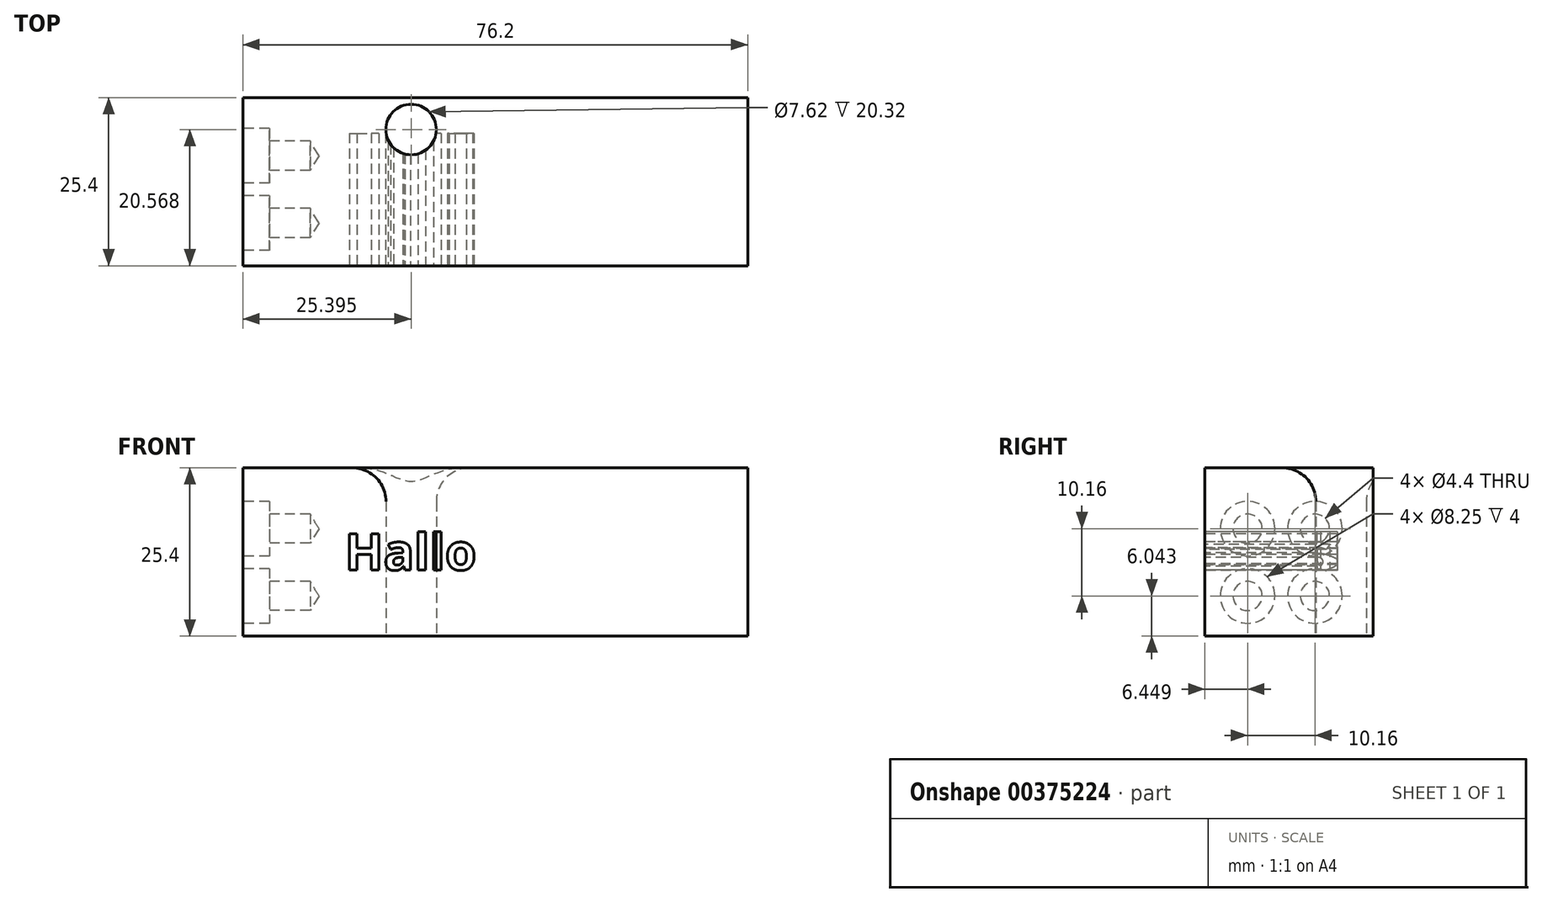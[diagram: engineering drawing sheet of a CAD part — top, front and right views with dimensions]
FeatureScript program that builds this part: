
annotation { "Feature Type Name" : "Feature", "Feature Type Description" : "" }
export const myFeature = defineFeature(function(context is Context, id is Id, definition is map)
    precondition{}
    {
        {
            var Q0;
            Q0=qCreatedBy(makeId("Top.planeOp"),FACE);
            var sketch = newSketch(context, id + "F0", { "sketchPlane" : qUnion([Q0])});
            skLineSegment(sketch, "E0", {"start": v(-63.01, -25.4) * mm, "end": v(-63.01, 0) * mm});
            skLineSegment(sketch, "E1", {"start": v(-63.01, 0) * mm, "end": v(13.19, 0) * mm});
            skLineSegment(sketch, "E2", {"start": v(13.19, 0) * mm, "end": v(13.19, -25.4) * mm});
            skLineSegment(sketch, "E3", {"start": v(13.19, -25.4) * mm, "end": v(-63.01, -25.4) * mm});
            skCircle(sketch, "E4", {"center": v(-37.61, -4.83) * mm, "radius": 3.81 * mm});
            skSolve(sketch);
        }
        {
            var Q0;
            Q0 = qSketchRegion(id + "F0", true);
            extrude(context, id + "F1", {"entities" : qUnion([Q0]), "depth" : 25.4 * mm});
        }
        {
            var Q0;
            Q0=makeQuery(id+"F1.opExtrude","SWEPT_FACE",FACE,{"disambiguationData":[OSD([sQuery(id+"F0.wireOp",EDGE,"E3")])]});
            var sketch = newSketch(context, id + "F2", { "sketchPlane" : qUnion([Q0])});
            skText(sketch, "E5", { "text": "Hallo", "fontName": "OpenSans-Bold.ttf"});
            skLineSegment(sketch, "E6", {"start": v(-63.01, 12.7) * mm, "end": v(13.19, 12.7) * mm, "construction": true});
            const initialGuessF2  = {"E5": [-0.04761, 0.00995, 1, 0, 0.0055]};
            skSetInitialGuess(sketch, initialGuessF2);
            skSolve(sketch);
        }
        {
            var Q0;
            Q0 = qSketchRegion(id + "F2", true);
            var Q1;
            Q1=makeQuery(id+"F1.opExtrude","SWEPT_FACE",FACE,{"disambiguationData":[OSD([sQuery(id+"F0.wireOp",EDGE,"E4")])]});
            extrude(context, id + "F3", {"entities" : qUnion([Q0]), "operationType" : NewBodyOperationType.REMOVE, "oppositeDirection" : true, "endBoundEntityFace" : qUnion([Q1]), "depth" : 20 * mm});
        }
        {
            var Q0;
            Q0=makeQuery(id+"F1.opExtrude","SWEPT_FACE",FACE,{"disambiguationData":[OSD([sQuery(id+"F0.wireOp",EDGE,"E0")])]});
            var sketch = newSketch(context, id + "F4", { "sketchPlane" : qUnion([Q0])});
            skPoint(sketch, "E7", {"position": v(8.8, 16.2) * mm});
            skPoint(sketch, "E8", {"position": v(18.95, 6.04) * mm});
            skPoint(sketch, "E9", {"position": v(8.8, 6.04) * mm});
            skPoint(sketch, "E10", {"position": v(18.95, 16.2) * mm});
            skLineSegment(sketch, "E11", {"start": v(18.95, 16.2) * mm, "end": v(18.95, 6.04) * mm, "construction": true});
            skLineSegment(sketch, "E12", {"start": v(18.95, 16.2) * mm, "end": v(8.8, 16.2) * mm, "construction": true});
            skSolve(sketch);
        }
        {
            var Q0;
            Q0=sQuery(id+"F4.wireOp",VERTEX,"E7");
            var Q1;
            Q1=sQuery(id+"F4.wireOp",VERTEX,"E8");
            var Q2;
            Q2=sQuery(id+"F4.wireOp",VERTEX,"E9");
            var Q3;
            Q3=sQuery(id+"F4.wireOp",VERTEX,"E10");
            var Q4;
            Q4=makeQuery(id+"F3.boolean.opBoolean","SPLIT",BODY,{"disambiguationData":[OD(1.0)],"derivedFrom":makeQuery(id+"F1.opExtrude","SWEPT_BODY",BODY,{"disambiguationData":[OSD([sQuery(id+"F0.wireOp",EDGE,"E0"),sQuery(id+"F0.wireOp",EDGE,"E1"),sQuery(id+"F0.wireOp",EDGE,"E2"),sQuery(id+"F0.wireOp",EDGE,"E3"),sQuery(id+"F0.wireOp",EDGE,"E4")])]})});
            hole(context, id + "F5", {"style" : HoleStyle.C_BORE, "endStyle" : HoleEndStyle.BLIND, "standardTappedOrClearance" : lookupTablePath({ "standard" : "ISO", "fit" : "Normal", "size" : "M4", "type" : "Clearance" }), "standardBlindInLast" : lookupTablePath({ "fit" : "Standard", "standard" : "ISO", "size" : "M4", "type" : "Clearance" }), "holeDiameter" : 4.4 * mm, "cBoreDiameter" : 8.25 * mm, "cBoreDepth" : 4 * mm, "holeDepth" : 10.16 * mm, "isTappedThrough" : true, "tappedDepth" : 12.7 * mm, "tapClearance" : 3, "locations" : qUnion([Q0, Q1, Q2, Q3]), "scope" : qUnion([Q4])});
        }
        {
            var Q0;
            Q0=makeQuery(id+"F1.opExtrude","CAP_EDGE",EDGE,{"disambiguationData":[OSD([sQuery(id+"F0.wireOp",EDGE,"E4")])],"isStart":false});
            fillet(context, id + "F6", {"entities" : qUnion([Q0]), "radius" : 5.08 * mm, "tangentPropagation" : true, "allowEdgeOverflow" : false});
        }
    });
